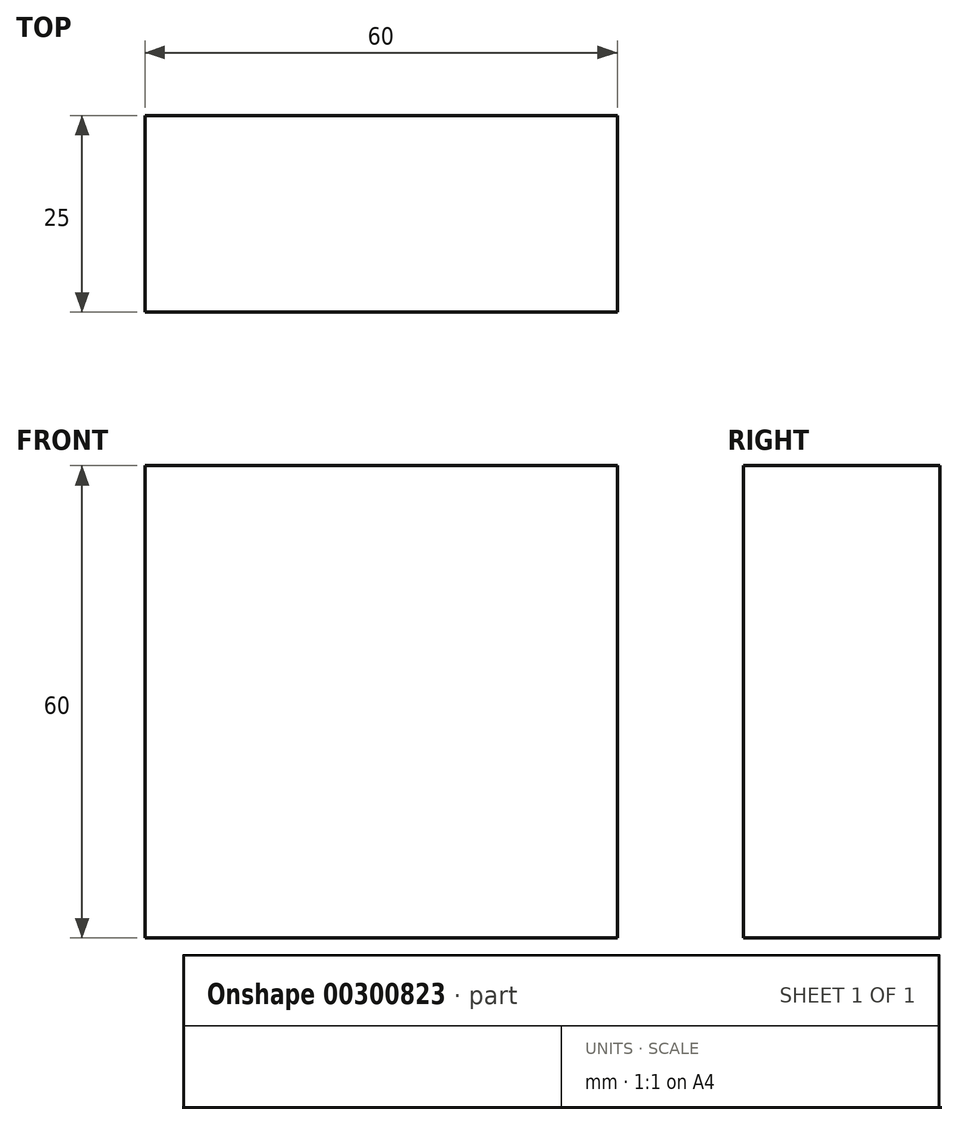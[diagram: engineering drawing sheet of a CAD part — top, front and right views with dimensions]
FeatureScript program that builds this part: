
annotation { "Feature Type Name" : "Feature", "Feature Type Description" : "" }
export const myFeature = defineFeature(function(context is Context, id is Id, definition is map)
    precondition{}
    {
        {
            var Q0;
            Q0=qCreatedBy(makeId("Front.planeOp"),FACE);
            var sketch = newSketch(context, id + "F0", { "sketchPlane" : qUnion([Q0])});
            skLineSegment(sketch, "E0.bottom", {"start": v(30, -30) * mm, "end": v(-30, -30) * mm});
            skLineSegment(sketch, "E0.top", {"start": v(30, 30) * mm, "end": v(-30, 30) * mm});
            skLineSegment(sketch, "E0.left", {"start": v(30, -30) * mm, "end": v(30, 30) * mm});
            skLineSegment(sketch, "E0.right", {"start": v(-30, -30) * mm, "end": v(-30, 30) * mm});
            skPoint(sketch, "E0.middle", {"position": v(0, 0) * mm});
            skPoint(sketch, "E1.end.orphan", {"position": v(-58.62, -46.21) * mm});
            skPoint(sketch, "E2.end.orphan", {"position": v(-58.62, -7.6) * mm});
            skLineSegment(sketch, "E3", {"start": v(-21.27, -30) * mm, "end": v(-21.27, -20) * mm});
            skLineSegment(sketch, "E4", {"start": v(-21.27, -20) * mm, "end": v(18.73, -20) * mm});
            skLineSegment(sketch, "E5", {"start": v(18.73, -20) * mm, "end": v(18.73, -30) * mm});
            skPoint(sketch, "E5.endSnap0", {"position": v(0, -30) * mm});
            skPoint(sketch, "E6.start.orphan", {"position": v(-58.62, -22.11) * mm});
            skLineSegment(sketch, "E7", {"start": v(-30, 22.2) * mm, "end": v(-12.66, 22.2) * mm});
            skLineSegment(sketch, "E8", {"start": v(-12.66, 22.2) * mm, "end": v(-12.66, -11.23) * mm});
            skLineSegment(sketch, "E9", {"start": v(-12.66, -11.23) * mm, "end": v(-30, -11.23) * mm});
            skSolve(sketch);
        }
        {
            var Q0;
            Q0 = qSketchRegion(id + "F0", true);
            extrude(context, id + "F1", {"entities" : qUnion([Q0]), "depth" : 25 * mm});
        }
    });
